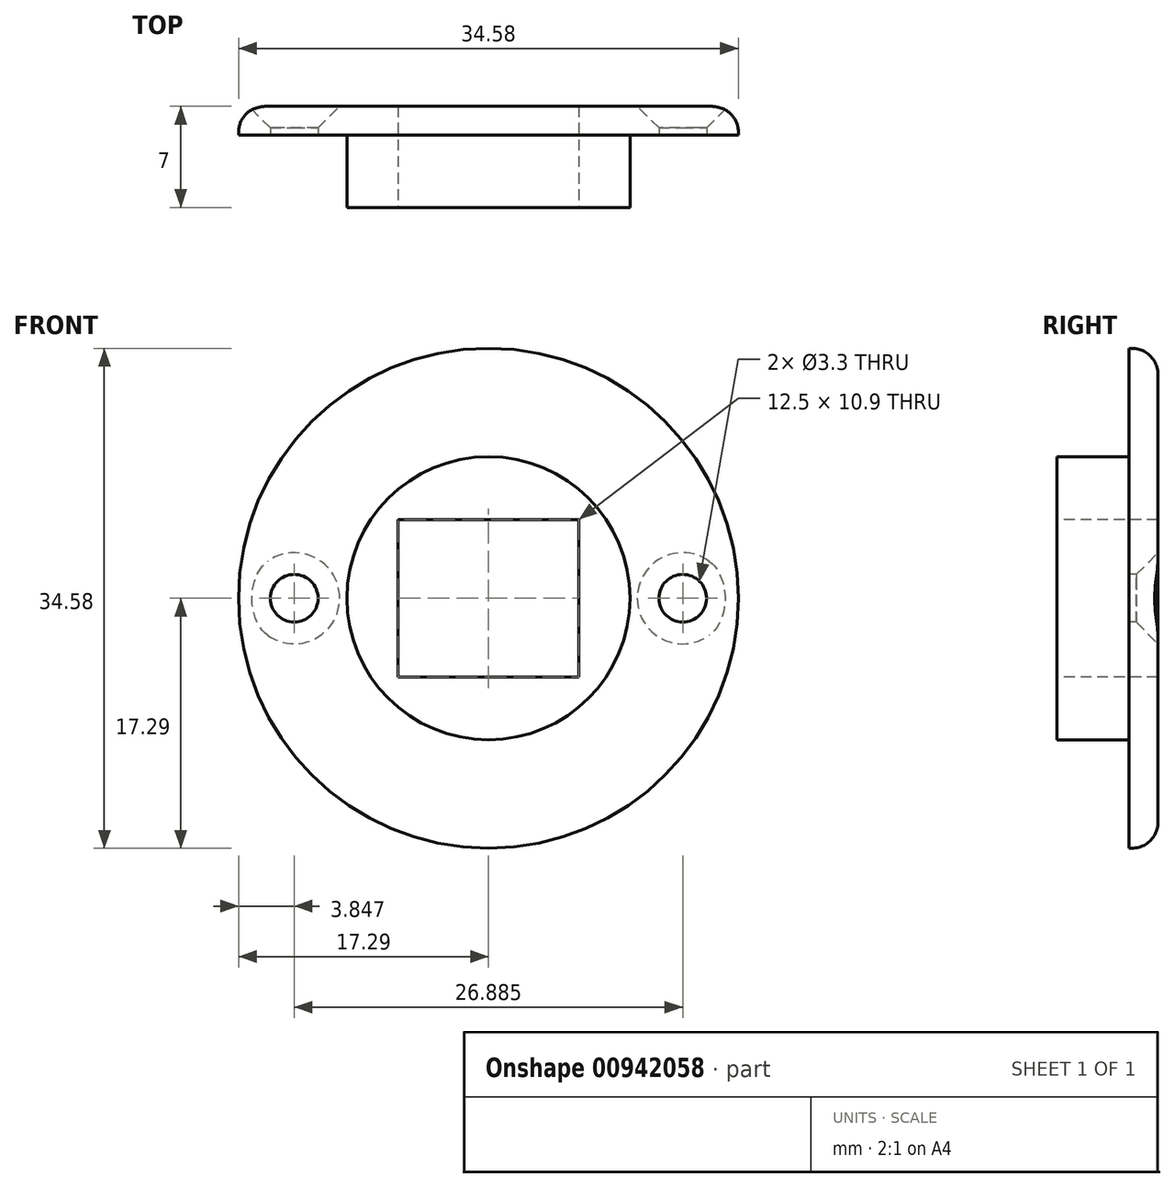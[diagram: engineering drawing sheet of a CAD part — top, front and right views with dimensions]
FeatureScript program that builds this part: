
annotation { "Feature Type Name" : "Feature", "Feature Type Description" : "" }
export const myFeature = defineFeature(function(context is Context, id is Id, definition is map)
    precondition{}
    {
        {
            var Q0;
            Q0=qCreatedBy(makeId("Front.planeOp"),FACE);
            var sketch = newSketch(context, id + "F0", { "sketchPlane" : qUnion([Q0])});
            skLineSegment(sketch, "E0.bottom", {"start": v(6.25, -5.45) * mm, "end": v(-6.25, -5.45) * mm});
            skLineSegment(sketch, "E0.top", {"start": v(6.25, 5.45) * mm, "end": v(-6.25, 5.45) * mm});
            skLineSegment(sketch, "E0.left", {"start": v(6.25, -5.45) * mm, "end": v(6.25, 5.45) * mm});
            skLineSegment(sketch, "E0.right", {"start": v(-6.25, -5.45) * mm, "end": v(-6.25, 5.45) * mm});
            skPoint(sketch, "E0.middle", {"position": v(0, 0) * mm});
            skCircle(sketch, "E1", {"center": v(0, 0) * mm, "radius": 8.3 * mm});
            skCircle(sketch, "E2.0", {"center": v(0, 0) * mm, "radius": 17.3 * mm});
            skLineSegment(sketch, "E3", {"start": v(-17.3, 0) * mm, "end": v(-8.3, 0) * mm, "construction": true});
            skLineSegment(sketch, "E4", {"start": v(0, 5.45) * mm, "end": v(0, 3.77) * mm, "construction": true});
            skCircle(sketch, "E5.0", {"center": v(0, 0) * mm, "radius": 9.8 * mm});
            skCircle(sketch, "E6", {"center": v(-13.44, 0) * mm, "radius": 1.65 * mm});
            skCircle(sketch, "E7.MirrorC", {"center": v(13.44, 0) * mm, "radius": 1.65 * mm});
            skSolve(sketch);
        }
        {
            var Q0;
            Q0=makeQuery(id+"F0.imprint","IMPRINT",FACE,{"disambiguationData":[TD([[makeQuery(id+"F0.imprint","IMPRINT",EDGE,{"derivedFrom":sQuery(id+"F0.wireOp",EDGE,"E2.0")}),1.0]])]});
            var Q1;
            Q1=makeQuery(id+"F0.imprint","IMPRINT",FACE,{"disambiguationData":[TD([[makeQuery(id+"F0.imprint","IMPRINT",EDGE,{"derivedFrom":sQuery(id+"F0.wireOp",EDGE,"E5.0")}),1.0]])]});
            var Q2;
            {var subQ0=sQuery(id+"F0.wireOp",EDGE,"E0.right");Q2=makeQuery(id+"F0.imprint","IMPRINT",FACE,{"disambiguationData":[TD([[makeQuery(id+"F0.imprint","IMPRINT",EDGE,{"derivedFrom":subQ0}),1.0]])]});}
            var Q3;
            {var subQ0=sQuery(id+"F0.wireOp",EDGE,"E0.top");Q3=makeQuery(id+"F0.imprint","IMPRINT",FACE,{"disambiguationData":[TD([[makeQuery(id+"F0.imprint","IMPRINT",EDGE,{"derivedFrom":subQ0}),-1.0]])]});}
            var Q4;
            {var subQ0=sQuery(id+"F0.wireOp",EDGE,"E0.left");Q4=makeQuery(id+"F0.imprint","IMPRINT",FACE,{"disambiguationData":[TD([[makeQuery(id+"F0.imprint","IMPRINT",EDGE,{"derivedFrom":subQ0}),-1.0]])]});}
            var Q5;
            {var subQ0=sQuery(id+"F0.wireOp",EDGE,"E0.bottom");Q5=makeQuery(id+"F0.imprint","IMPRINT",FACE,{"disambiguationData":[TD([[makeQuery(id+"F0.imprint","IMPRINT",EDGE,{"derivedFrom":subQ0}),1.0]])]});}
            extrude(context, id + "F1", {"entities" : qUnion([Q0, Q1, Q2, Q3, Q4, Q5]), "oppositeDirection" : true, "depth" : 2 * mm, "offsetDistance" : 25 * mm});
        }
        {
            var Q0;
            Q0=makeQuery(id+"F0.imprint","IMPRINT",FACE,{"disambiguationData":[TD([[makeQuery(id+"F0.imprint","IMPRINT",EDGE,{"derivedFrom":sQuery(id+"F0.wireOp",EDGE,"E5.0")}),1.0]])]});
            var Q1;
            {var subQ0=sQuery(id+"F0.wireOp",EDGE,"E0.right");Q1=makeQuery(id+"F0.imprint","IMPRINT",FACE,{"disambiguationData":[TD([[makeQuery(id+"F0.imprint","IMPRINT",EDGE,{"derivedFrom":subQ0}),1.0]])]});}
            var Q2;
            {var subQ0=sQuery(id+"F0.wireOp",EDGE,"E0.top");Q2=makeQuery(id+"F0.imprint","IMPRINT",FACE,{"disambiguationData":[TD([[makeQuery(id+"F0.imprint","IMPRINT",EDGE,{"derivedFrom":subQ0}),-1.0]])]});}
            var Q3;
            {var subQ0=sQuery(id+"F0.wireOp",EDGE,"E0.left");Q3=makeQuery(id+"F0.imprint","IMPRINT",FACE,{"disambiguationData":[TD([[makeQuery(id+"F0.imprint","IMPRINT",EDGE,{"derivedFrom":subQ0}),-1.0]])]});}
            var Q4;
            {var subQ0=sQuery(id+"F0.wireOp",EDGE,"E0.bottom");Q4=makeQuery(id+"F0.imprint","IMPRINT",FACE,{"disambiguationData":[TD([[makeQuery(id+"F0.imprint","IMPRINT",EDGE,{"derivedFrom":subQ0}),1.0]])]});}
            extrude(context, id + "F2", {"entities" : qUnion([Q0, Q1, Q2, Q3, Q4]), "operationType" : NewBodyOperationType.ADD, "depth" : 5 * mm, "offsetDistance" : 25 * mm});
        }
        {
            var Q0;
            Q0=makeQuery(id+"F1.opExtrude","CAP_EDGE",EDGE,{"disambiguationData":[OSD([sQuery(id+"F0.wireOp",EDGE,"E7.MirrorC")])],"isStart":false});
            var Q1;
            Q1=makeQuery(id+"F1.opExtrude","CAP_EDGE",EDGE,{"disambiguationData":[OSD([sQuery(id+"F0.wireOp",EDGE,"E6")])],"isStart":false});
            chamfer(context, id + "F3", {"entities" : qUnion([Q0, Q1]), "width" : 1.5 * mm, "tangentPropagation" : true});
        }
        {
            var Q0;
            Q0=makeQuery(id+"F1.opExtrude","CAP_EDGE",EDGE,{"disambiguationData":[OSD([sQuery(id+"F0.wireOp",EDGE,"E2.0")])],"isStart":false});
            fillet(context, id + "F4", {"entities" : qUnion([Q0]), "radius" : 1.8 * mm, "tangentPropagation" : true, "allowEdgeOverflow" : false});
        }
    });
